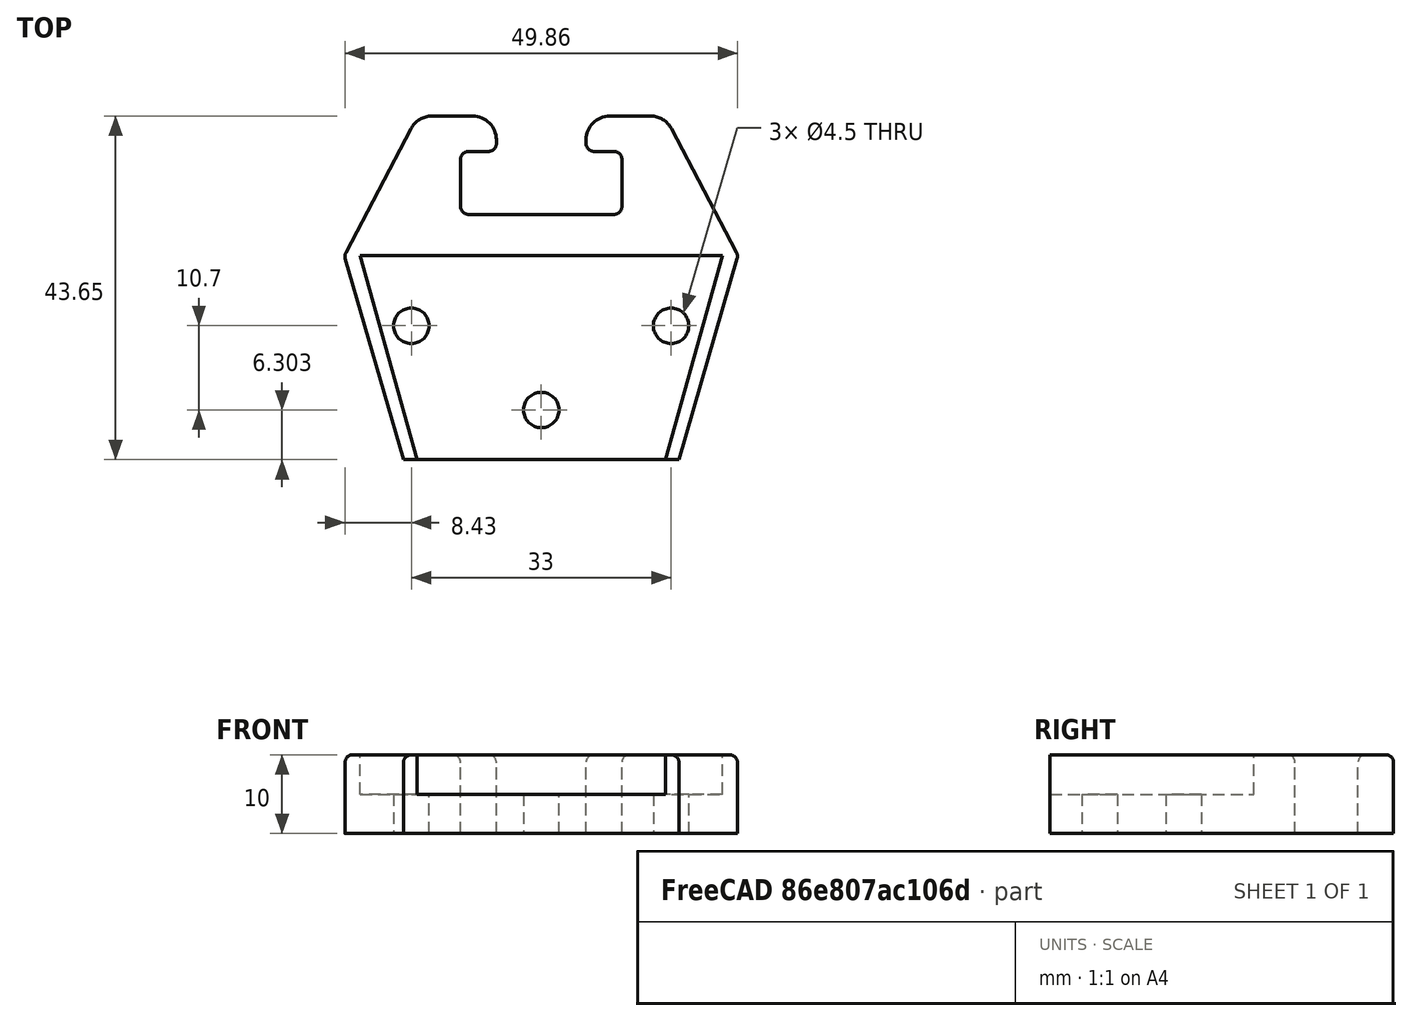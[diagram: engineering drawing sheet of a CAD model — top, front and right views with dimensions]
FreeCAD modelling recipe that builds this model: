
FCSTD DOCUMENT  (FreeCAD 0.20R29410 (Git))
Label: drawer_glide
License: All rights reserved
LicenseURL: http://en.wikipedia.org/wiki/All_rights_reserved
objects: PartDesign::Fillet×3, Sketcher::SketchObject×2, PartDesign::Pad×1, PartDesign::Pocket×1, PartDesign::Body×1, App::Part×1, Mesh::Feature×1
note: 13 computed .brp shape members not serialized (recipe doc carries the construction recipe); baked Part::Feature solids carry a one-line shape summary decoded from their .brp

FEATURE [Sketcher::SketchObject] Sketch
  FullyConstrained = true
  MapMode = 5
  Support = -> [XY_Plane001]
  sketch-geometry (17):
    g0: LineSegment StartX=-17.5 StartY=-25.9374 StartZ=0 EndX=17.5 EndY=-25.9374 EndZ=0
    g1: LineSegment StartX=17.5 StartY=-25.9374 StartZ=0 EndX=25 EndY=0 EndZ=0
    g2: LineSegment StartX=25 StartY=0 StartZ=0 EndX=15.7 EndY=17.7062 EndZ=0
    g3: LineSegment StartX=15.7 StartY=17.7062 StartZ=0 EndX=5.7 EndY=17.7062 EndZ=0
    g4: LineSegment StartX=5.7 StartY=17.7062 StartZ=0 EndX=5.7 EndY=13.2062 EndZ=0
    g5: LineSegment StartX=5.7 StartY=13.2062 StartZ=0 EndX=10.25 EndY=13.2062 EndZ=0
    g6: LineSegment StartX=10.25 StartY=13.2062 StartZ=0 EndX=10.25 EndY=5.20621 EndZ=0
    g7: LineSegment StartX=10.25 StartY=5.20621 StartZ=0 EndX=-10.25 EndY=5.20621 EndZ=0
    g8: LineSegment StartX=-10.25 StartY=5.20621 StartZ=0 EndX=-10.25 EndY=13.2062 EndZ=0
    g9: LineSegment StartX=-10.25 StartY=13.2062 StartZ=0 EndX=-5.7 EndY=13.2062 EndZ=0
    g10: LineSegment StartX=-5.7 StartY=13.2062 StartZ=0 EndX=-5.7 EndY=17.7062 EndZ=0
    g11: LineSegment StartX=-5.7 StartY=17.7062 StartZ=0 EndX=-15.7 EndY=17.7062 EndZ=0
    g12: LineSegment StartX=-15.7 StartY=17.7062 StartZ=0 EndX=-25 EndY=0 EndZ=0
    g13: LineSegment StartX=-25 StartY=0 StartZ=0 EndX=-17.5 EndY=-25.9374 EndZ=0
    g14: Circle CenterX=0 CenterY=-19.6374 CenterZ=0 NormalX=0 NormalY=0 NormalZ=1 AngleXU=0 Radius=2.25
    g15: Circle CenterX=-16.5 CenterY=-8.93742 CenterZ=0 NormalX=0 NormalY=0 NormalZ=1 AngleXU=0 Radius=2.25
    g16: Circle CenterX=16.5 CenterY=-8.93742 CenterZ=0 NormalX=0 NormalY=0 NormalZ=1 AngleXU=0 Radius=2.25
  constraints (49):
    c: Horizontal(g0)
    c: Coincident(g1,g0)
    c: PointOnObject(g1,g-1)
    c: Coincident(g1,g2)
    c: Coincident(g2,g3)
    c: Horizontal(g3)
    c: Coincident(g3,g4)
    c: Vertical(g4)
    c: Coincident(g4,g5)
    c: Horizontal(g5)
    c: Coincident(g5,g6)
    c: Coincident(g6,g7)
    c: Horizontal(g7)
    c: Coincident(g7,g8)
    c: Vertical(g8)
    c: Coincident(g8,g9)
    c: Horizontal(g9)
    c: Coincident(g9,g10)
    c: Vertical(g10)
    c: Coincident(g10,g11)
    c: Horizontal(g11)
    c: Coincident(g11,g12)
    c: Coincident(g12,g13)
    c: Coincident(g13,g0)
    c: Equal(g10,g4)
    c: Equal(g11,g3)
    c: Equal(g12,g2)
    c: Equal(g13,g1)
    c: Equal(g9,g5)
    c: Equal(g8,g6)
    c: Vertical(g6)
    c: DistanceX(g0,g0) = 35
    c: Distance(g13) = 27
    c: Distance(g2) = 20
    c: Distance(g3) = 10
    c: Distance(g7) = 20.5
    c: Distance(g12,g1) = 50
    c: Symmetric(g12,g1,g-1)
    c: Distance(g10,g3) = 11.4
    c: Distance(g4) = 4.5
    c: Distance(g8) = 8
    c: PointOnObject(g14,g-2)
    c: Equal(g15,g14)
    c: Equal(g14,g16)
    c: Diameter(g16) = 4.5
    c: Symmetric(g15,g16,g-2)
    c: Distance(g14,g0) = 6.3
    c: Distance(g15,g16) = 33
    c: Distance(g15,g0) = 17
FEATURE [PartDesign::Pad] Pad
  Direction = (0,0,1)
  Length = 10
  Length2 = 10
  Profile = -> Sketch
  ReferenceAxis = -> Sketch [N_Axis]
  Type = 0
FEATURE [Sketcher::SketchObject] Sketch001
  AttachmentOffset = pos=(0,0,5) rot=(0,0,1;0rad)
  FullyConstrained = true
  MapMode = 5
  Placement = pos=(0,0,5) rot=(0,0,1;0rad)
  Support = -> [XY_Plane001]
  sketch-geometry (4):
    g0: LineSegment StartX=-15.5 StartY=-26.9768 StartZ=0 EndX=-23 EndY=0 EndZ=0
    g1: LineSegment StartX=-23 StartY=0 StartZ=0 EndX=23 EndY=4e-15 EndZ=0
    g2: LineSegment StartX=23 StartY=4e-15 StartZ=0 EndX=15.5 EndY=-26.9768 EndZ=0
    g3: LineSegment StartX=15.5 StartY=-26.9768 StartZ=0 EndX=-15.5 EndY=-26.9768 EndZ=0
  constraints (12):
    c: PointOnObject(g0,g-1)
    c: Coincident(g0,g1)
    c: Coincident(g1,g2)
    c: Coincident(g2,g3)
    c: Coincident(g3,g0)
    c: Horizontal(g3)
    c: Equal(g0,g2)
    c: Symmetric(g0,g1,g-2)
    c: Symmetric(g0,g2,g-2)
    c: Distance(g3) = 31
    c: Distance(g1) = 46
    c: Distance(g0) = 28
FEATURE [PartDesign::Pocket] Pocket
  BaseFeature = -> Pad
  Direction = (0,0,-1)
  Length = 10
  Length2 = 5
  Profile = -> Sketch001
  ReferenceAxis = -> Sketch001 [N_Axis]
  Reversed = true
  Type = 0
FEATURE [PartDesign::Fillet] Fillet
  Base = -> Pocket [Edge51,Edge60,Edge59,Edge52]
  BaseFeature = -> Pocket
  Radius = 3
  SupportTransform = false
  UseAllEdges = false
FEATURE [PartDesign::Fillet] Fillet001
  Base = -> Fillet [Edge59,Edge41,Edge23,Edge39,Edge49,Edge53,Edge57,Edge45]
  BaseFeature = -> Fillet
  Radius = 1
  SupportTransform = false
  UseAllEdges = false
FEATURE [PartDesign::Fillet] Fillet002
  Base = -> Fillet001 [Edge38]
  BaseFeature = -> Fillet001
  Radius = 1
  SupportTransform = false
  UseAllEdges = false
FEATURE [PartDesign::Body] Body
  Group = -> [Sketch,Pad,Sketch001,Pocket,Fillet,Fillet001,Fillet002]
  Origin = -> Origin001
  Tip = -> Fillet002
FEATURE [App::Part] Part
  Group = -> [Body]
  Origin = -> Origin
FEATURE [Mesh::Feature] Mesh  label="Body (Meshed)"
